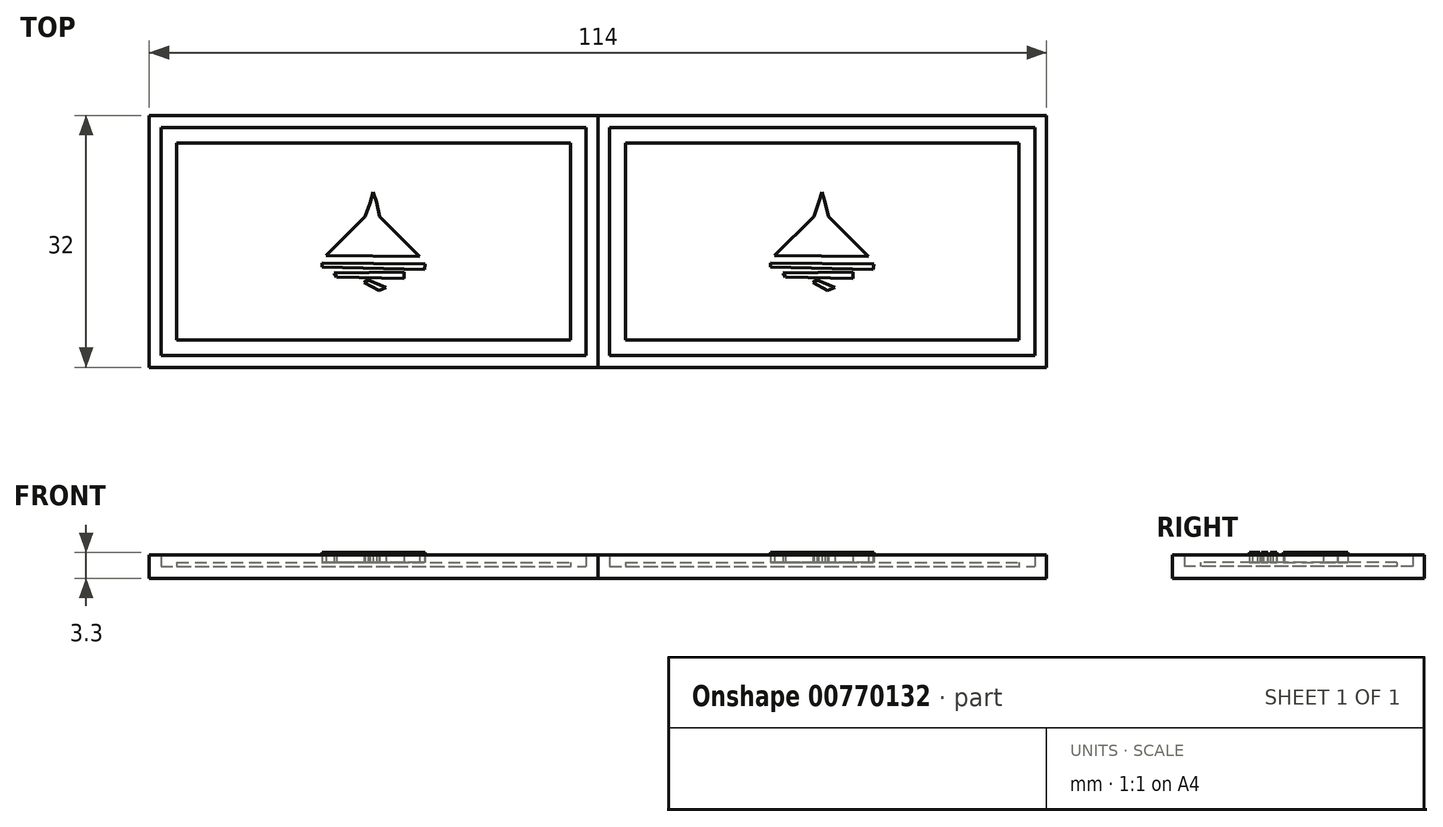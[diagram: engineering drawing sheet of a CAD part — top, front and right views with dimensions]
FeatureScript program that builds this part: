
annotation { "Feature Type Name" : "Feature", "Feature Type Description" : "" }
export const myFeature = defineFeature(function(context is Context, id is Id, definition is map)
    precondition{}
    {
        {
            var Q0;
            Q0=qCreatedBy(makeId("Top.planeOp"),FACE);
            var sketch = newSketch(context, id + "F0", { "sketchPlane" : qUnion([Q0])});
            skLineSegment(sketch, "E0.bottom", {"start": v(-25, 12.5) * mm, "end": v(25, 12.5) * mm});
            skLineSegment(sketch, "E0.top", {"start": v(-25, -12.5) * mm, "end": v(25, -12.5) * mm});
            skLineSegment(sketch, "E0.left", {"start": v(-25, 12.5) * mm, "end": v(-25, -12.5) * mm});
            skLineSegment(sketch, "E0.right", {"start": v(25, 12.5) * mm, "end": v(25, -12.5) * mm});
            skLineSegment(sketch, "E1.bottom", {"start": v(-27, 14.5) * mm, "end": v(27, 14.5) * mm});
            skLineSegment(sketch, "E1.top", {"start": v(-27, -14.5) * mm, "end": v(27, -14.5) * mm});
            skLineSegment(sketch, "E1.left", {"start": v(-27, 14.5) * mm, "end": v(-27, -14.5) * mm});
            skLineSegment(sketch, "E1.right", {"start": v(27, 14.5) * mm, "end": v(27, -14.5) * mm});
            skLineSegment(sketch, "E2.bottom", {"start": v(-28.5, 16) * mm, "end": v(28.5, 16) * mm});
            skLineSegment(sketch, "E2.top", {"start": v(-28.5, -16) * mm, "end": v(28.5, -16) * mm});
            skLineSegment(sketch, "E2.left", {"start": v(-28.5, 16) * mm, "end": v(-28.5, -16) * mm});
            skLineSegment(sketch, "E2.right", {"start": v(28.5, 16) * mm, "end": v(28.5, -16) * mm});
            skSolve(sketch);
        }
        {
            var Q0;
            Q0=makeQuery(id+"F0.imprint","IMPRINT",FACE,{"disambiguationData":[TD([[makeQuery(id+"F0.imprint","IMPRINT",EDGE,{"derivedFrom":sQuery(id+"F0.wireOp",EDGE,"E0.bottom")}),-1.0]])]});
            extrude(context, id + "F1", {"entities" : qUnion([Q0]), "depth" : 2 * mm, "offsetDistance" : 25 * mm});
        }
        {
            var Q0;
            Q0=makeQuery(id+"F1.opExtrude","CAP_FACE",FACE,{"disambiguationData":[OSD([sQuery(id+"F0.wireOp",EDGE,"E0.bottom"),sQuery(id+"F0.wireOp",EDGE,"E0.top"),sQuery(id+"F0.wireOp",EDGE,"E0.left"),sQuery(id+"F0.wireOp",EDGE,"E0.right")])],"isStart":false});
            var sketch = newSketch(context, id + "F2", { "sketchPlane" : qUnion([Q0])});
            skLineSegment(sketch, "E3", {"start": v(-0.67, -4.9) * mm, "end": v(1.6, -5.84) * mm});
            skLineSegment(sketch, "E4", {"start": v(1.6, -5.84) * mm, "end": v(0.67, -6.25) * mm});
            skLineSegment(sketch, "E5", {"start": v(0.67, -6.25) * mm, "end": v(-1.19, -5.22) * mm});
            skLineSegment(sketch, "E6", {"start": v(-1.19, -5.22) * mm, "end": v(-0.67, -4.9) * mm});
            skLineSegment(sketch, "E7", {"start": v(-5.01, -3.98) * mm, "end": v(3.87, -3.87) * mm});
            skLineSegment(sketch, "E8", {"start": v(3.87, -3.87) * mm, "end": v(3.87, -4.7) * mm});
            skLineSegment(sketch, "E9", {"start": v(3.87, -4.7) * mm, "end": v(-4.7, -4.5) * mm});
            skLineSegment(sketch, "E10", {"start": v(-4.7, -4.5) * mm, "end": v(-5.01, -3.98) * mm});
            skLineSegment(sketch, "E11", {"start": v(-6.56, -2.74) * mm, "end": v(6.56, -2.84) * mm});
            skLineSegment(sketch, "E12", {"start": v(6.56, -2.84) * mm, "end": v(6.46, -3.56) * mm});
            skLineSegment(sketch, "E13", {"start": v(6.46, -3.56) * mm, "end": v(-6.56, -3.25) * mm});
            skLineSegment(sketch, "E14", {"start": v(-6.56, -3.25) * mm, "end": v(-6.56, -2.74) * mm});
            skLineSegment(sketch, "E15", {"start": v(-0.05, 6.25) * mm, "end": v(-0.46, 4.9) * mm});
            skLineSegment(sketch, "E16", {"start": v(-0.46, 4.9) * mm, "end": v(-1.08, 3.15) * mm});
            skLineSegment(sketch, "E17", {"start": v(-1.08, 3.15) * mm, "end": v(-6.04, -1.8) * mm});
            skLineSegment(sketch, "E18", {"start": v(-6.04, -1.8) * mm, "end": v(5.84, -1.91) * mm});
            skLineSegment(sketch, "E19", {"start": v(5.84, -1.91) * mm, "end": v(0.77, 3.15) * mm});
            skLineSegment(sketch, "E20", {"start": v(0.77, 3.15) * mm, "end": v(0.36, 5.01) * mm});
            skLineSegment(sketch, "E21", {"start": v(0.36, 5.01) * mm, "end": v(-0.05, 6.25) * mm});
            skSolve(sketch);
        }
        {
            var Q0;
            Q0 = qSketchRegion(id + "F2", true);
            extrude(context, id + "F3", {"entities" : qUnion([Q0]), "operationType" : NewBodyOperationType.ADD, "depth" : 1.3 * mm, "offsetDistance" : 25 * mm});
        }
        {
            var Q0;
            Q0=makeQuery(id+"F0.imprint","IMPRINT",FACE,{"disambiguationData":[TD([[makeQuery(id+"F0.imprint","IMPRINT",EDGE,{"derivedFrom":sQuery(id+"F0.wireOp",EDGE,"E0.bottom")}),1.0]])]});
            extrude(context, id + "F4", {"entities" : qUnion([Q0]), "operationType" : NewBodyOperationType.ADD, "depth" : 1.5 * mm, "offsetDistance" : 25 * mm});
        }
        {
            var Q0;
            Q0=makeQuery(id+"F0.imprint","IMPRINT",FACE,{"disambiguationData":[TD([[makeQuery(id+"F0.imprint","IMPRINT",EDGE,{"derivedFrom":sQuery(id+"F0.wireOp",EDGE,"E1.bottom")}),1.0]])]});
            extrude(context, id + "F5", {"entities" : qUnion([Q0]), "operationType" : NewBodyOperationType.ADD, "depth" : 3 * mm, "offsetDistance" : 25 * mm});
        }
        {
            var Q0;
            Q0=makeQuery(id+"F1.opExtrude","SWEPT_BODY",BODY,{"disambiguationData":[OSD([sQuery(id+"F0.wireOp",EDGE,"E0.bottom"),sQuery(id+"F0.wireOp",EDGE,"E0.top"),sQuery(id+"F0.wireOp",EDGE,"E0.left"),sQuery(id+"F0.wireOp",EDGE,"E0.right")])]});
            transform(context, id + "F6", {"entities" : qUnion([Q0]), "transformType" : TransformType.TRANSLATION_3D, "dx" : 57 * mm, "dy" : 0 * mm, "dz" : 0 * mm, "makeCopy" : true});
        }
    });
